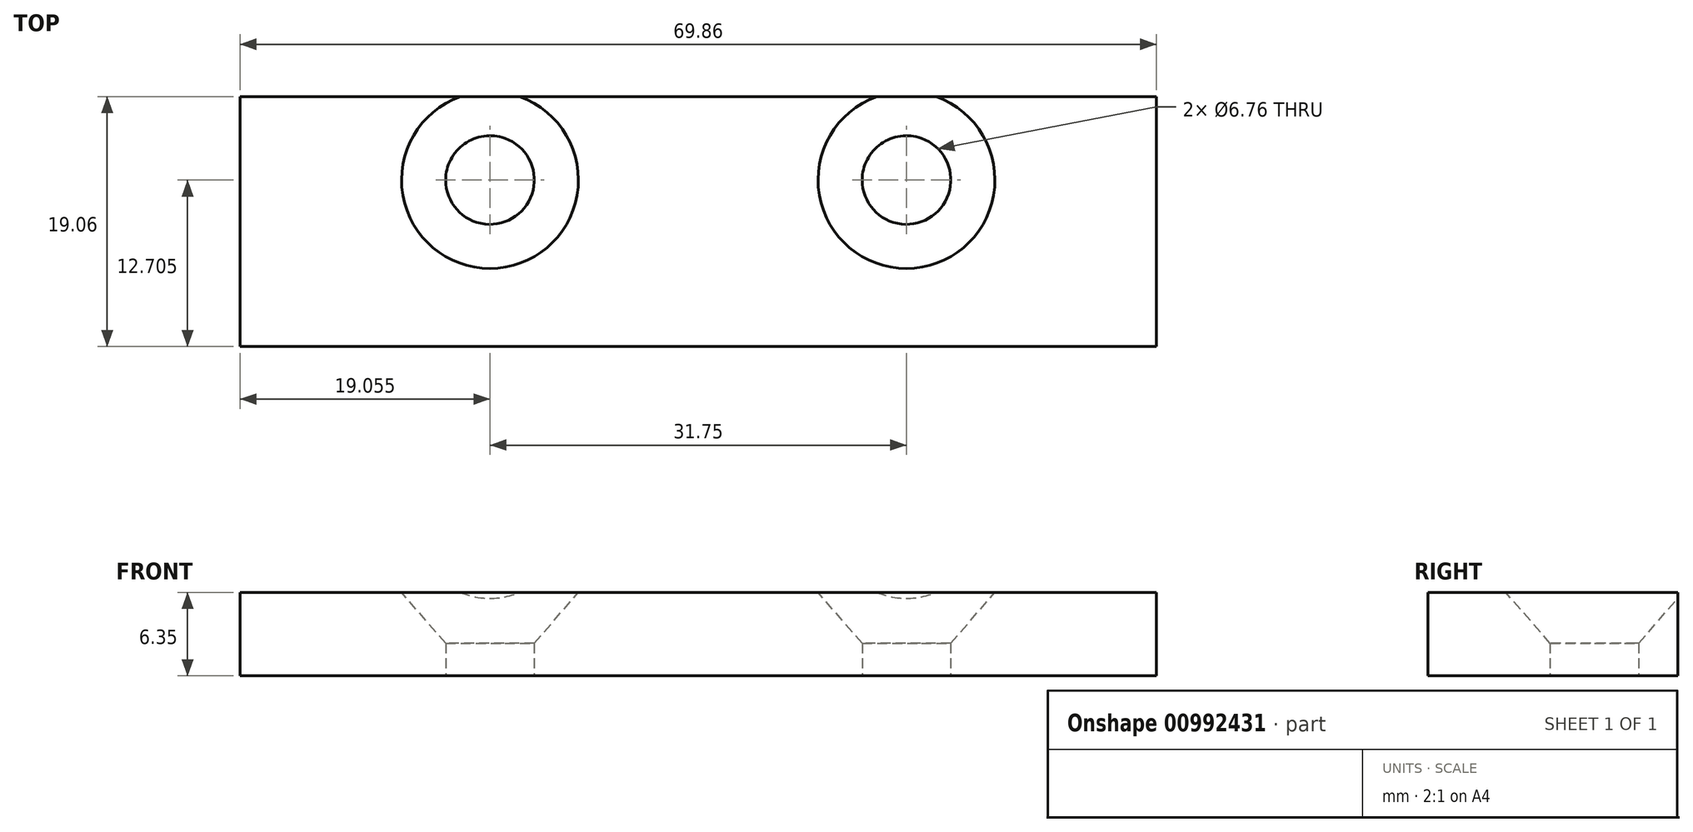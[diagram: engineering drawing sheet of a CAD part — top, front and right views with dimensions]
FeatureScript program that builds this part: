
annotation { "Feature Type Name" : "Feature", "Feature Type Description" : "" }
export const myFeature = defineFeature(function(context is Context, id is Id, definition is map)
    precondition{}
    {
        {
            var Q0;
            Q0=qCreatedBy(makeId("Top.planeOp"),FACE);
            var sketch = newSketch(context, id + "F0", { "sketchPlane" : qUnion([Q0])});
            skLineSegment(sketch, "E0.bottom", {"start": v(34.93, 9.52) * mm, "end": v(-34.93, 9.52) * mm});
            skLineSegment(sketch, "E0.top", {"start": v(34.93, -9.53) * mm, "end": v(-34.93, -9.53) * mm});
            skLineSegment(sketch, "E0.left", {"start": v(34.93, 9.52) * mm, "end": v(34.93, -9.53) * mm});
            skLineSegment(sketch, "E0.right", {"start": v(-34.93, 9.52) * mm, "end": v(-34.93, -9.53) * mm});
            skPoint(sketch, "E0.middle", {"position": v(0, 0) * mm});
            skCircle(sketch, "E1", {"center": v(-15.88, 3.17) * mm, "radius": 3.57 * mm});
            skCircle(sketch, "E2", {"center": v(15.88, 3.17) * mm, "radius": 3.57 * mm});
            skSolve(sketch);
        }
        {
            var Q0;
            Q0=makeQuery(id+"F0.imprint","IMPRINT",FACE,{"disambiguationData":[TD([[makeQuery(id+"F0.imprint","IMPRINT",EDGE,{"derivedFrom":sQuery(id+"F0.wireOp",EDGE,"E1")}),1.0]])]});
            var Q1;
            Q1=makeQuery(id+"F0.imprint","IMPRINT",FACE,{"disambiguationData":[TD([[makeQuery(id+"F0.imprint","IMPRINT",EDGE,{"derivedFrom":sQuery(id+"F0.wireOp",EDGE,"E2")}),1.0]])]});
            var Q2;
            Q2=makeQuery(id+"F0.imprint","IMPRINT",FACE,{"disambiguationData":[TD([[makeQuery(id+"F0.imprint","IMPRINT",EDGE,{"derivedFrom":sQuery(id+"F0.wireOp",EDGE,"E0.bottom")}),1.0]])]});
            extrude(context, id + "F1", {"entities" : qUnion([Q0, Q1, Q2]), "oppositeDirection" : true, "depth" : 6.35 * mm, "offsetDistance" : 25.4 * mm});
        }
        {
            var Q0;
            Q0=sQuery(id+"F0.wireOp",VERTEX,"E1.center");
            var Q1;
            Q1=sQuery(id+"F0.wireOp",VERTEX,"E2.center");
            var Q2;
            Q2=makeQuery(id+"F1.opExtrude","SWEPT_BODY",BODY,{"disambiguationData":[OSD([sQuery(id+"F0.wireOp",EDGE,"E0.bottom"),sQuery(id+"F0.wireOp",EDGE,"E0.top"),sQuery(id+"F0.wireOp",EDGE,"E0.left"),sQuery(id+"F0.wireOp",EDGE,"E0.right")])]});
            hole(context, id + "F2", {"style" : HoleStyle.C_SINK, "endStyle" : HoleEndStyle.THROUGH, "standardTappedOrClearance" : lookupTablePath({ "fit" : "Close (ASME)", "standard" : "ANSI", "size" : "1/4", "type" : "Clearance" }), "standardBlindInLast" : lookupTablePath({ "fit" : "Close", "standard" : "ANSI", "engagement" : "75%", "pitch" : "20 tpi", "size" : "1/4", "type" : "Clearance & tapped" }), "holeDiameter" : 6.76 * mm, "cSinkDiameter" : 13.5 * mm, "cSinkAngle" : 82 * degree, "majorDiameter" : 6.35 * mm, "isTappedThrough" : true, "tappedDepth" : 12.7 * mm, "tapClearance" : 3, "locations" : qUnion([Q0, Q1]), "scope" : qUnion([Q2]), "startStyle" : HoleStartStyle.SKETCH});
        }
    });
